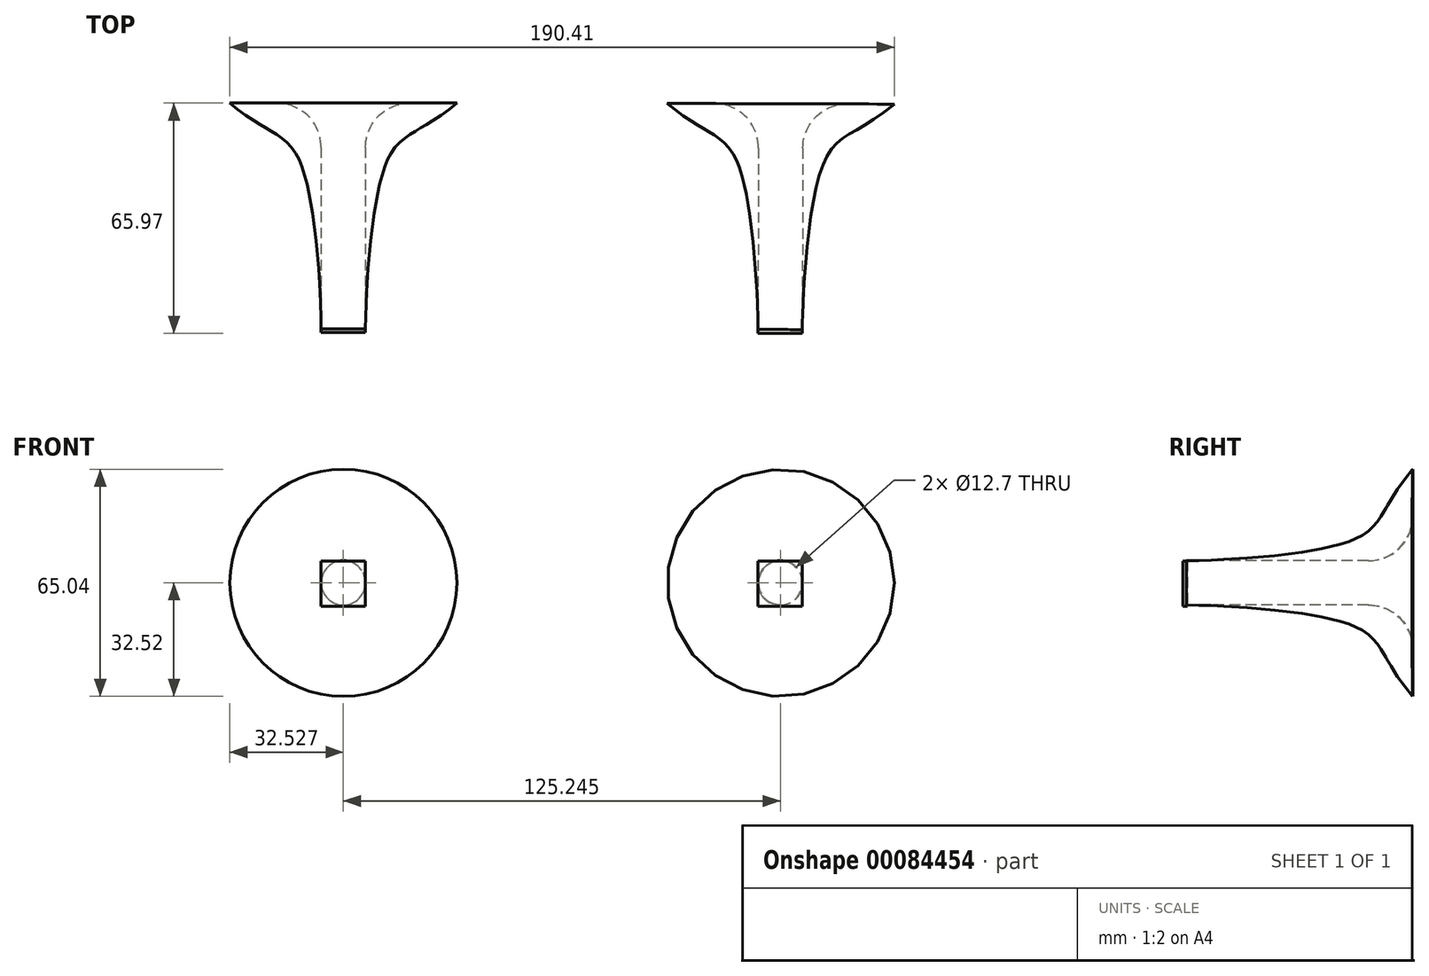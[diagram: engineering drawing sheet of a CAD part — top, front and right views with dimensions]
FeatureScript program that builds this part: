
annotation { "Feature Type Name" : "Feature", "Feature Type Description" : "" }
export const myFeature = defineFeature(function(context is Context, id is Id, definition is map)
    precondition{}
    {
        {
            var Q0;
            Q0=qCreatedBy(makeId("Top.planeOp"),FACE);
            var sketch = newSketch(context, id + "F0", { "sketchPlane" : qUnion([Q0])});
            skFitSpline(sketch, "E0", {"points": [v(-29.47, 78.93) * mm, v(-49.6, 62.12) * mm, v(-55.64, 14.22) * mm], "startDerivative": vector(-74.59, -63.29) * mm, "endDerivative": vector(0, -34.53) * mm});
            skLineSegment(sketch, "E1", {"start": v(-55.64, 14.22) * mm, "end": v(-55.64, 78.93) * mm});
            skLineSegment(sketch, "E2", {"start": v(-55.64, 78.93) * mm, "end": v(-29.47, 78.93) * mm});
            skLineSegment(sketch, "E3", {"start": v(-62, 14.22) * mm, "end": v(-62, 78.93) * mm});
            skLineSegment(sketch, "E4.bottom", {"start": v(-62, 14.22) * mm, "end": v(-55.64, 14.22) * mm});
            skLineSegment(sketch, "E4.top", {"start": v(-62, 13.16) * mm, "end": v(-55.64, 13.16) * mm});
            skLineSegment(sketch, "E4.left", {"start": v(-62, 14.22) * mm, "end": v(-62, 13.16) * mm});
            skLineSegment(sketch, "E4.right", {"start": v(-55.64, 14.22) * mm, "end": v(-55.64, 13.16) * mm});
            skLineSegment(sketch, "E5.MirrorCS", {"start": v(-62, 14.22) * mm, "end": v(-68.34, 14.22) * mm});
            skLineSegment(sketch, "E6.MirrorCS", {"start": v(-62, 13.16) * mm, "end": v(-68.34, 13.16) * mm});
            skLineSegment(sketch, "E7.MirrorCS", {"start": v(-68.34, 14.22) * mm, "end": v(-68.34, 13.16) * mm});
            skLineSegment(sketch, "E8.MirrorCS", {"start": v(63.18, 14.04) * mm, "end": v(69.53, 14.02) * mm});
            skLineSegment(sketch, "E9.MirrorCS", {"start": v(69.53, 14.02) * mm, "end": v(69.52, 12.96) * mm});
            skLineSegment(sketch, "E10.MirrorCS", {"start": v(63.17, 12.97) * mm, "end": v(69.52, 12.96) * mm});
            skLineSegment(sketch, "E11.MirrorCS", {"start": v(63.18, 14.04) * mm, "end": v(63.17, 12.97) * mm});
            skLineSegment(sketch, "E12.MirrorCS", {"start": v(63.18, 14.04) * mm, "end": v(56.83, 14.06) * mm});
            skLineSegment(sketch, "E13.MirrorCS", {"start": v(63.17, 12.97) * mm, "end": v(56.82, 13) * mm});
            skLineSegment(sketch, "E14.MirrorCS", {"start": v(56.83, 14.06) * mm, "end": v(56.82, 13) * mm});
            skLineSegment(sketch, "E15.MirrorCS", {"start": v(63.18, 14.04) * mm, "end": v(63.36, 78.75) * mm});
            skFitSpline(sketch, "E16.MirrorCS", {"points": [v(30.84, 78.85) * mm, v(50.91, 61.97) * mm, v(56.83, 14.06) * mm], "startDerivative": vector(74.4, -63.5) * mm, "endDerivative": vector(-0.1, -34.53) * mm});
            skLineSegment(sketch, "E17.MirrorCS", {"start": v(56.83, 14.06) * mm, "end": v(57.01, 78.77) * mm});
            skFitSpline(sketch, "E18.MirrorCS", {"points": [v(30.84, 78.85) * mm, v(50.91, 61.97) * mm, v(56.83, 14.06) * mm], "startDerivative": vector(74.4, -63.5) * mm, "endDerivative": vector(-0.1, -34.53) * mm});
            skLineSegment(sketch, "E19.MirrorCS", {"start": v(57.01, 78.77) * mm, "end": v(30.84, 78.85) * mm});
            skSolve(sketch);
        }
        {
            var Q0;
            Q0=makeQuery(id+"F0.imprint","IMPRINT",FACE,{"disambiguationData":[TD([[makeQuery(id+"F0.imprint","IMPRINT",EDGE,{"derivedFrom":sQuery(id+"F0.wireOp",EDGE,"E0")}),-1.0]])]});
            var Q1;
            Q1=sQuery(id+"F0.wireOp",EDGE,"E3");
            revolve(context, id + "F1", {"entities" : qUnion([Q0]), "axis" : qUnion([Q1]), "revolveType" : RevolveType.FULL});
        }
        {
            var Q0;
            Q0=makeQuery(id+"F1.opRevolve","SWEPT_EDGE",EDGE,{"disambiguationData":[OSD([sQuery(id+"F0.wireOp",EDGE,"E1"),sQuery(id+"F0.wireOp",EDGE,"E2")])]});
            fillet(context, id + "F2", {"entities" : qUnion([Q0]), "radius" : 12.7 * mm, "tangentPropagation" : true, "allowEdgeOverflow" : false});
        }
        {
            var Q0;
            Q0=makeQuery(id+"F0.imprint","IMPRINT",FACE,{"disambiguationData":[TD([[makeQuery(id+"F0.imprint","IMPRINT",EDGE,{"derivedFrom":sQuery(id+"F0.wireOp",EDGE,"E4.bottom")}),-1.0]])]});
            var Q1;
            Q1=makeQuery(id+"F0.imprint","IMPRINT",FACE,{"disambiguationData":[TD([[makeQuery(id+"F0.imprint","IMPRINT",EDGE,{"derivedFrom":sQuery(id+"F0.wireOp",EDGE,"E4.left")}),-1.0]])]});
            var Q2;
            Q2=makeQuery(id+"F0.imprint","IMPRINT",FACE,{"disambiguationData":[TD([[makeQuery(id+"F0.imprint","IMPRINT",EDGE,{"derivedFrom":sQuery(id+"F0.wireOp",EDGE,"E11.MirrorCS")}),-1.0]])]});
            var Q3;
            Q3=makeQuery(id+"F0.imprint","IMPRINT",FACE,{"disambiguationData":[TD([[makeQuery(id+"F0.imprint","IMPRINT",EDGE,{"derivedFrom":sQuery(id+"F0.wireOp",EDGE,"E8.MirrorCS")}),-1.0]])]});
            extrude(context, id + "F3", {"entities" : qUnion([Q0, Q1, Q2, Q3]), "depth" : 6.26 * mm, "hasSecondDirection" : true, "secondDirectionOppositeDirection" : true, "secondDirectionDepth" : 6.72 * mm});
        }
        {
            var Q0;
            Q0=makeQuery(id+"F0.imprint","IMPRINT",FACE,{"disambiguationData":[TD([[makeQuery(id+"F0.imprint","IMPRINT",EDGE,{"derivedFrom":sQuery(id+"F0.wireOp",EDGE,"E17.MirrorCS")}),1.0]])]});
            var Q1;
            Q1=sQuery(id+"F0.wireOp",EDGE,"E15.MirrorCS");
            revolve(context, id + "F4", {"entities" : qUnion([Q0]), "axis" : qUnion([Q1]), "revolveType" : RevolveType.FULL});
        }
        {
            var Q0;
            Q0=makeQuery(id+"F4.opRevolve","SWEPT_EDGE",EDGE,{"disambiguationData":[OSD([sQuery(id+"F0.wireOp",EDGE,"E17.MirrorCS"),sQuery(id+"F0.wireOp",EDGE,"E19.MirrorCS")])]});
            var Q1;
            Q1=makeQuery(id+"F2.opFillet","BLEND_FACE",FACE,{"disambiguationData":[OSD([sQuery(id+"F0.wireOp",EDGE,"E1"),sQuery(id+"F0.wireOp",EDGE,"E2")])]});
            fillet(context, id + "F5", {"entities" : qUnion([Q0, Q1]), "radius" : 12.7 * mm, "tangentPropagation" : true, "allowEdgeOverflow" : false});
        }
    });
